# Revit family: Plumbing-Flushometer-Sloan-Valve-SOLIS-8152_
name_source: partatom
category: Plumbing Fixtures
units: mm (PartAtom-declared; Revit-internal decimal feet)

## family parameters
Cut with Voids When Loaded = Yes
Host = Face
OmniClass Number = 23.45.05.14.99
OmniClass Title = Other Sanitary Washing Plumbing Fixtures
Part Type = Normal
Room Calculation Point = No
Round Connector Dimension = Use Diameter
Shared = No

## types (4) — shared parameters
Assembly Code = D2020300
CW Connection = Yes
Centerline of Supply from Top of Fixture = 14 1/2"
Centerline of Supply to Centerline of Valve = 4 3/4"
Default Elevation = 0"
Edition number = 1
HW Connection = No
Keynote = 15410
L Dimension = 4 3/4"
Manufacturer = Sloan Valve
Operating Water Pressure = 15 – 80 PSI (103 – 552 kPa)
Product Material = Sloan Valve - Finish - Rough Brass
Product data url = https://bimobject.com
URL = www.sloanvalve.com
Valve Pressure Drop = 0.00 psi
Vent Connection = No
Waste Connection = No
Water Inlet Connection Description = Water Inlet Connection
Water Inlet Connection Diameter = 1"
zero-valued in all types: CWFU, HWFU, WFU

## per-type parameters (varying)
| type | Description | Flush Rate | Part Number |
| SOLIS 8152-1.28-TMO-SWB | 1.28 gpf, Rough Brass Finish, Fixture Connection Rear Spud, Single Flush, True Mechanical Override, Solar, Small Wall Box, SOLIS® Concealed Sensor Water Closet Hydraulic Flushometer. | 1.28 gpf (4.8 Lpf) | 3370060 |
| SOLIS 8152-1.6-TMO-SWB | 1.6 gpf, Rough Brass Finish, Fixture Connection Rear Spud, Single Flush, True Mechanical Override, Solar, Small Wall Box, SOLIS® Concealed Sensor Water Closet Hydraulic Flushometer. | 1.6 gpf (6.0 Lpf) | 3370061 |
| SOLIS 8152-1.28-TMO-L/BOX | 1.28 gpf, Rough Brass Finish, Fixture Connection Rear Spud, Single Flush, True Mechanical Override, Solar, Less Wall Box, SOLIS® Concealed Sensor Water Closet Hydraulic Flushometer. | 1.28 gpf (4.8 Lpf) | 3370065 |
| SOLIS 8152-1.6-TMO-L/BOX | 1.6 gpf, Rough Brass Finish, Fixture Connection Rear Spud, Single Flush, True Mechanical Override, Solar, Less Wall Box, SOLIS® Concealed Sensor Water Closet Hydraulic Flushometer. | 1.6 gpf (6.0 Lpf) | 3370064 |

note: column(s) folded — value = type name in every type: Model

## geometry (parser evidence)
native form markers: Sweep x7
no freeform markers — native parametric forms only
